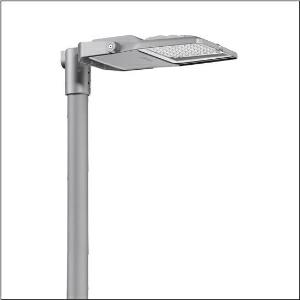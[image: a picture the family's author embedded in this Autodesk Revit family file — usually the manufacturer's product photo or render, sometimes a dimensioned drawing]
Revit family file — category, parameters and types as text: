
# Revit family: floodlight_fl_21_iq_mini___pl43_5xa7771d4a3a_2bc1
name_source: partatom
category: Lighting Fixtures
units: mm (PartAtom-declared; Revit-internal decimal feet)

## family parameters
Cut with Voids When Loaded = No
Host = Face
Light Source = No
Part Type = Normal
Room Calculation Point = No
Round Connector Dimension = Use Diameter
Shared = No

## types (1)
- --- (1 x LED, 19090 lm, 143 W, 4000K)
    Apparent Load = 143 VA
    CIE Flux Codes = 27 78 99 100 100
    Color Rendering = 70
    Color Temperature = 4000K
    Default Elevation = 1800 mm
    Description = Floodlight FL 21 iQ mini, floodlight, primary light control with lens, of PMMA, primary optical cover: protective disc, of toughened safety glass, transparent, light distribution: PL43, light emission: direct distribution, installation type: surface-mounted, LED, High Power LED, rated luminous flux: 19.090lm, luminous efficacy: 134lm/W, light colour: 740, colour temperature: 4000K, control: Auto-Match, Temp-Guard, Lumen-Switch, Night-Set, Smart-Wire, Light-Fading, Desk-Remote (wireless, voltage-free reading and setting of iQ features in the workshop via application-optimized NFC function/RFID function), optimised constant luminous flux control (CLO 2.0), with terminal, 6-pole, mains connection: 220..240V, AC, 50/60Hz, start of lifetime: 143W, end of service life: 152W, reduction: 61W, luminaire housing, of diecast aluminium, powder-coated, Siteco® metallic grey (DB 702S), corrosivity category C5 mid according to DIN EN ISO 12944, sealing non-destructively replaceable, please order mast flange separately, mast bracket, of steel, galvanised, powder-coated, Siteco® metallic grey (DB 702S), protection rating (complete): IP66, insulation class (complete): insulation class II (safety insulation), certification: CE, ENEC, VDE, protection symbol: D, impact resistance: IK08, permissible operating ambient temperature: -40..+40°C, permissible operating ambient temperature for outdoor applications: -40..+50°C, standard: DIN EN 12944, LABS conformity tested according to VDMA 24364:2018-05, packaging unit: 1 piece

Light Distribution: PL43
    Height = 70 mm
    Lamp = 1 x LED
    Lamp Light Flux = 19090 lm
    Lamp Power = 143 W
    Lamp count = 1
    Length = 485 mm
    Luminous efficacy = 133 lm/W
    Manufacturer = Siteco
    ModVariant = No
    Model = 5XA7771D4A3A
    Number of Poles = 1
    OnlyDefault = Yes
    Power Factor = 1
    Product Name = Floodlight FL 21 iQ mini | PL43
    Product group = floodlight | pylon annexe
    ProductGroupID = 6200
    Protection Class = Protection class II
    Protection Degree = IP 66
    RLX_Detail_Level = 1
    RLX_Emergency_Light_Flux = 0 lm
    RLX_Emergency_Type = 0
    RLX_Emergency_Type_DB = No
    RlxData = <blob elided: 101493 chars, md5=76c76a9d>
    Socket = socket
    Standby Power = 0 W
    System Light Flux = 19090 lm
    System Power = 143 W
    Type Comments = factory setting: luminous flux: 100 % | dim-lin: 254 | 730 mA
    Type Image = l_1007125.jpg
    URL = http://relux.com
    VarID = @adj_111905
    Voltage = 0 V
    Weight = 0.00 kg
    Width = 337 mm

## geometry (parser evidence)
native form markers: Blend x4, Sweep x12
no freeform markers — native parametric forms only
